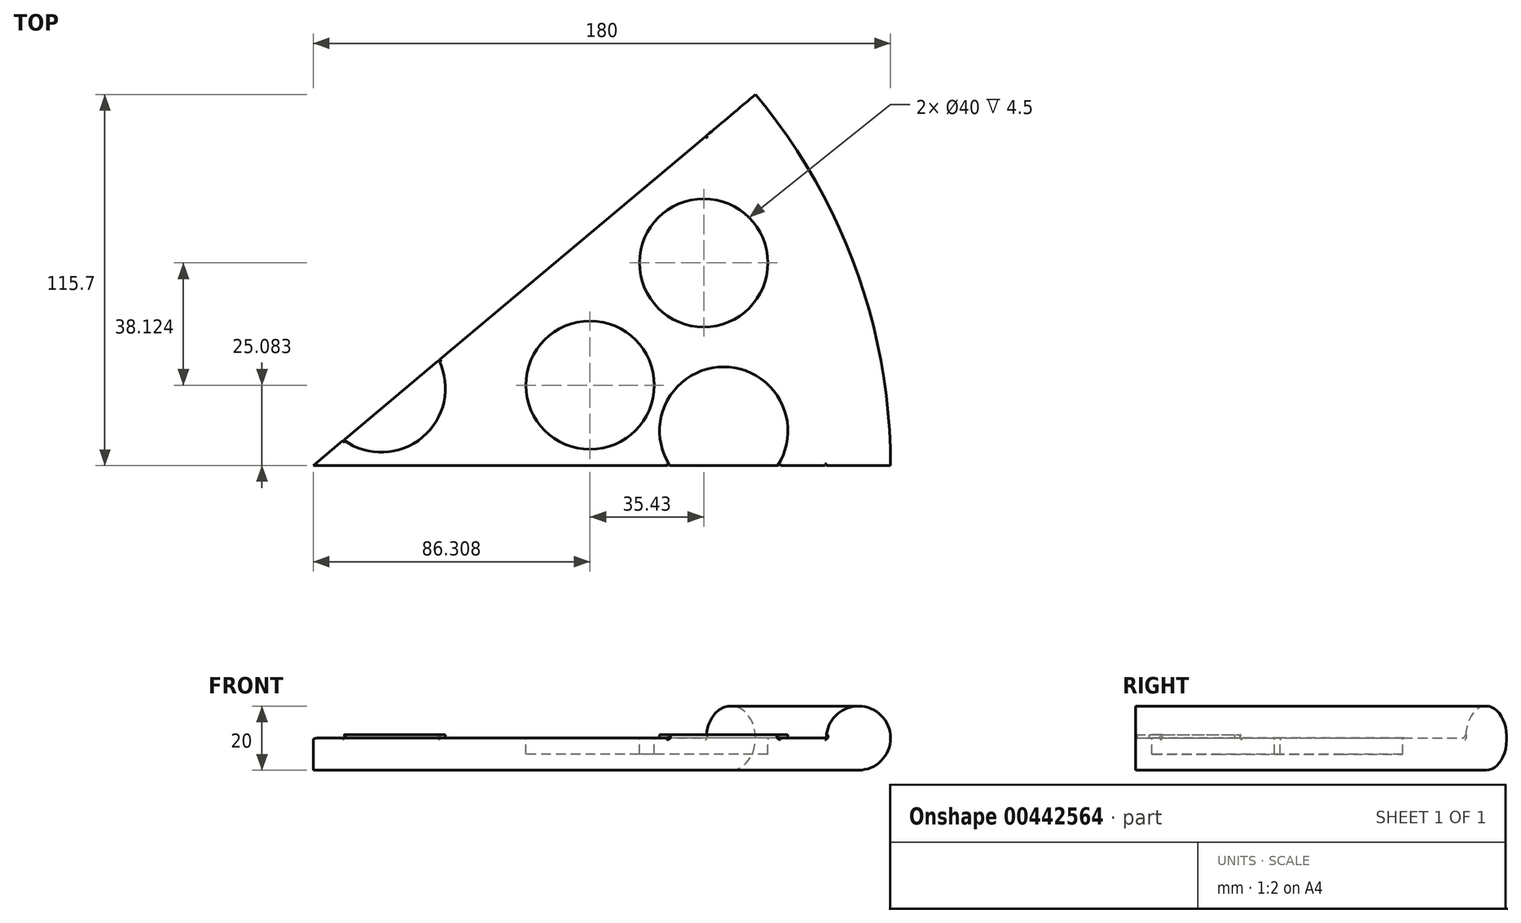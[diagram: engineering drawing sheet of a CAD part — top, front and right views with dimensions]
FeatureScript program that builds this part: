
annotation { "Feature Type Name" : "Feature", "Feature Type Description" : "" }
export const myFeature = defineFeature(function(context is Context, id is Id, definition is map)
    precondition{}
    {
        {
            var Q0;
            Q0=qCreatedBy(makeId("Top.planeOp"),FACE);
            var sketch = newSketch(context, id + "F0", { "sketchPlane" : qUnion([Q0])});
            skLineSegment(sketch, "E0", {"start": v(0, 0) * mm, "end": v(130.23, 109.27) * mm});
            skLineSegment(sketch, "E1", {"start": v(0, 0) * mm, "end": v(170, 0) * mm});
            skArc(sketch, "E2", {"start": v(170, 0) * mm, "mid": v(159.75, 58.14) * mm, "end": v(130.23, 109.27) * mm});
            skSolve(sketch);
        }
        {
            var Q0;
            Q0 = qSketchRegion(id + "F0", true);
            extrude(context, id + "F1", {"entities" : qUnion([Q0]), "depth" : 10 * mm});
        }
        {
            var Q0;
            Q0=makeQuery(id+"F1.opExtrude","SWEPT_FACE",FACE,{"disambiguationData":[OSD([sQuery(id+"F0.wireOp",EDGE,"E1")])]});
            var sketch = newSketch(context, id + "F2", { "sketchPlane" : qUnion([Q0])});
            skCircle(sketch, "E3", {"center": v(170, 10) * mm, "radius": 10 * mm});
            skSolve(sketch);
        }
        {
            var Q0;
            Q0 = qSketchRegion(id + "F2", true);
            var Q1;
            Q1=makeQuery(id+"F1.opExtrude","CAP_EDGE",EDGE,{"disambiguationData":[OSD([sQuery(id+"F0.wireOp",EDGE,"E2")])],"isStart":false});
            sweep(context, id + "F3", {"operationType" : NewBodyOperationType.ADD, "profiles" : qUnion([Q0]), "path" : qUnion([Q1])});
        }
        {
            var Q0;
            Q0=makeQuery(id+"F1.opExtrude","CAP_FACE",FACE,{"disambiguationData":[OSD([sQuery(id+"F0.wireOp",EDGE,"E0"),sQuery(id+"F0.wireOp",EDGE,"E1"),sQuery(id+"F0.wireOp",EDGE,"E2")])],"isStart":false});
            var sketch = newSketch(context, id + "F4", { "sketchPlane" : qUnion([Q0])});
            skCircle(sketch, "E4", {"center": v(121.74, 63.2) * mm, "radius": 20 * mm});
            skCircle(sketch, "E5", {"center": v(86.3, 25.08) * mm, "radius": 20 * mm});
            skSolve(sketch);
        }
        {
            var Q0;
            Q0 = qSketchRegion(id + "F4", true);
            extrude(context, id + "F5", {"entities" : qUnion([Q0]), "operationType" : NewBodyOperationType.REMOVE, "oppositeDirection" : true, "depth" : 5 * mm});
        }
        {
            var Q0;
            Q0=makeQuery(id+"F1.opExtrude","CAP_FACE",FACE,{"disambiguationData":[OSD([sQuery(id+"F0.wireOp",EDGE,"E0"),sQuery(id+"F0.wireOp",EDGE,"E1"),sQuery(id+"F0.wireOp",EDGE,"E2")])],"isStart":false});
            var sketch = newSketch(context, id + "F6", { "sketchPlane" : qUnion([Q0])});
            skArc(sketch, "E6", {"start": v(144.82, 0) * mm, "mid": v(127.98, 30.79) * mm, "end": v(111.14, 0) * mm});
            skArc(sketch, "E7", {"start": v(9.48, 7.96) * mm, "mid": v(34.06, 8.84) * mm, "end": v(39.2, 32.9) * mm});
            skLineSegment(sketch, "E8", {"start": v(39.2, 32.9) * mm, "end": v(9.48, 7.96) * mm});
            skLineSegment(sketch, "E9", {"start": v(144.82, 0) * mm, "end": v(111.14, 0) * mm});
            skSolve(sketch);
        }
        {
            var Q0;
            Q0 = qSketchRegion(id + "F6", true);
            extrude(context, id + "F7", {"entities" : qUnion([Q0]), "operationType" : NewBodyOperationType.ADD, "depth" : 1 * mm});
        }
        {
            var Q0;
            Q0=makeQuery(id+"F1.opExtrude","CAP_FACE",FACE,{"disambiguationData":[OSD([sQuery(id+"F0.wireOp",EDGE,"E0"),sQuery(id+"F0.wireOp",EDGE,"E1"),sQuery(id+"F0.wireOp",EDGE,"E2")])],"isStart":false});
            fillet(context, id + "F8", {"entities" : qUnion([Q0]), "radius" : .5 * mm, "tangentPropagation" : true, "allowEdgeOverflow" : false});
        }
    });
